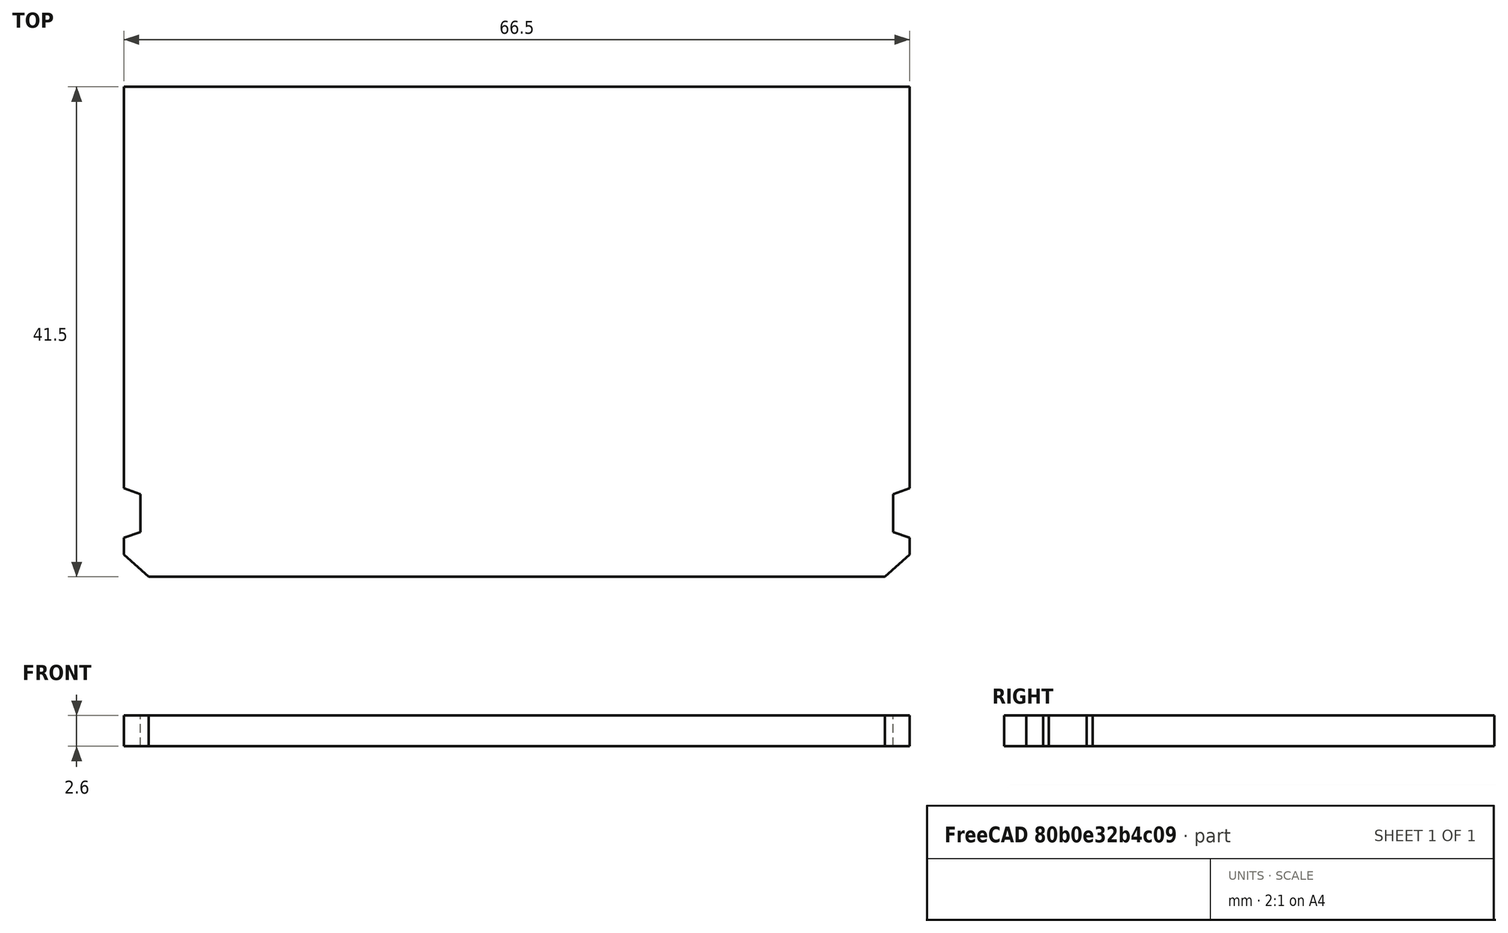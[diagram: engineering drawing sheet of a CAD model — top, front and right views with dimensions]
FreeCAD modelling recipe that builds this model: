
FCSTD DOCUMENT  (FreeCAD 0.21R33771 (Git))
Label: shell_v2
License: All rights reserved
LicenseURL: http://en.wikipedia.org/wiki/All_rights_reserved
objects: Sketcher::SketchObject×1, PartDesign::Pad×1, PartDesign::Body×1
note: 4 computed .brp shape members not serialized (recipe doc carries the construction recipe); baked Part::Feature solids carry a one-line shape summary decoded from their .brp

FEATURE [Sketcher::SketchObject] Sketch  label="base_sketch"
  FullyConstrained = true
  MapMode = 5
  Support = -> [XY_Plane]
  sketch-geometry (17):
    g0: LineSegment StartX=-33.25 StartY=20.75 StartZ=0 EndX=33.25 EndY=20.75 EndZ=0
    g1: LineSegment StartX=33.25 StartY=20.75 StartZ=0 EndX=33.25 EndY=-13.25 EndZ=0
    g2: LineSegment StartX=33.25 StartY=-13.25 StartZ=0 EndX=31.85 EndY=-13.75 EndZ=0
    g3: LineSegment StartX=31.85 StartY=-13.75 StartZ=0 EndX=31.85 EndY=-16.95 EndZ=0
    g4: LineSegment StartX=31.85 StartY=-16.95 StartZ=0 EndX=33.25 EndY=-17.45 EndZ=0
    g5: LineSegment StartX=33.25 StartY=-17.45 StartZ=0 EndX=33.25 EndY=-18.85 EndZ=0
    g6: LineSegment StartX=33.25 StartY=-18.85 StartZ=0 EndX=31.15 EndY=-20.75 EndZ=0
    g7: LineSegment StartX=-31.15 StartY=-20.75 StartZ=0 EndX=-33.25 EndY=-18.85 EndZ=0
    g8: LineSegment StartX=-33.25 StartY=-18.85 StartZ=0 EndX=-33.25 EndY=-17.45 EndZ=0
    g9: LineSegment StartX=-33.25 StartY=-17.45 StartZ=0 EndX=-31.85 EndY=-16.95 EndZ=0
    g10: LineSegment StartX=-31.85 StartY=-16.95 StartZ=0 EndX=-31.85 EndY=-13.75 EndZ=0
    g11: LineSegment StartX=-31.85 StartY=-13.75 StartZ=0 EndX=-33.25 EndY=-13.25 EndZ=0
    g12: LineSegment StartX=-33.25 StartY=-13.25 StartZ=0 EndX=-33.25 EndY=20.75 EndZ=0
    g13: LineSegment StartX=-31.15 StartY=-20.75 StartZ=0 EndX=31.15 EndY=-20.75 EndZ=0
    g14: LineSegment StartX=0 StartY=-20.75 StartZ=0 EndX=0 EndY=0 EndZ=0
    g15: LineSegment StartX=0 StartY=0 StartZ=0 EndX=0 EndY=20.75 EndZ=0
    g16: LineSegment StartX=-33.25 StartY=-17.45 StartZ=0 EndX=-33.25 EndY=-13.25 EndZ=0
  constraints (43):
    c: Coincident(g0,g1)
    c: Vertical(g1)
    c: Coincident(g1,g2)
    c: Coincident(g2,g3)
    c: Coincident(g3,g4)
    c: Coincident(g4,g5)
    c: Vertical(g5)
    c: Coincident(g5,g6)
    c: Coincident(g7,g8)
    c: Coincident(g8,g9)
    c: Coincident(g9,g10)
    c: Vertical(g10)
    c: Coincident(g10,g11)
    c: Coincident(g11,g12)
    c: Coincident(g12,g0)
    c: Symmetric(g0,g0,g-2)
    c: Symmetric(g11,g1,g-2)
    c: Symmetric(g3,g9,g-2)
    c: Symmetric(g8,g4,g-2)
    c: Symmetric(g7,g5,g-2)
    c: DistanceX(g0,g0) = 66.5
    c: DistanceY(g7,g0) = 41.5
    c: Symmetric(g10,g2,g-2)
    c: Coincident(g13,g7)
    c: Coincident(g13,g6)
    c: Symmetric(g7,g6,g-2)
    c: PointOnObject(g14,g13)
    c: Vertical(g14)
    c: Coincident(g15,g14)
    c: PointOnObject(g15,g0)
    c: Vertical(g15)
    c: Coincident(g14,g-1)
    c: Coincident(g16,g8)
    c: Vertical(g16)
    c: Coincident(g16,g11)
    c: DistanceY(g10,g10) = 3.2
    c: DistanceY(g11,g11) = 0.5
    c: DistanceY(g9,g9) = 0.5
    c: DistanceY(g8,g8) = 1.4
    c: DistanceY(g7,g8) = 3.3
    c: DistanceX(g7,g7) = 2.1
    c: DistanceX(g11,g11) = 1.4
    c: Equal(g15,g14)
FEATURE [PartDesign::Pad] Pad
  Direction = (0,0,1)
  Length = 2.6
  Length2 = 100
  Profile = -> Sketch
  Type = 0
FEATURE [PartDesign::Body] Body
  Group = -> [Sketch,Pad]
  Origin = -> Origin
  Tip = -> Pad
